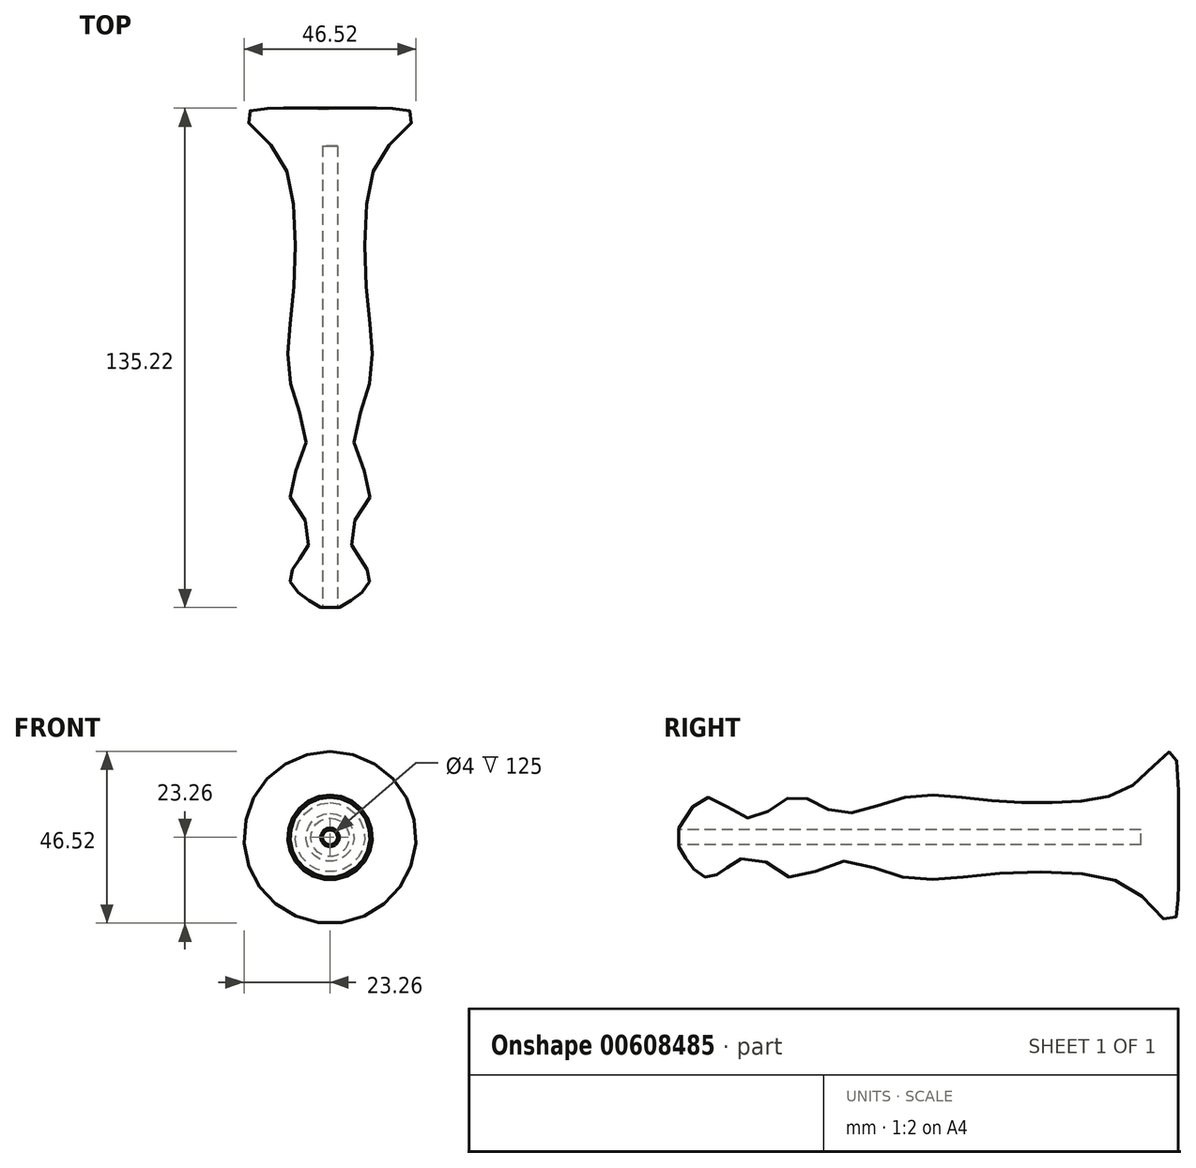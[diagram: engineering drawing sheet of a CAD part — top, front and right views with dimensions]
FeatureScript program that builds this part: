
annotation { "Feature Type Name" : "Feature", "Feature Type Description" : "" }
export const myFeature = defineFeature(function(context is Context, id is Id, definition is map)
    precondition{}
    {
        {
            var Q0;
            Q0=qCreatedBy(makeId("Right.planeOp"),FACE);
            var sketch = newSketch(context, id + "F0", { "sketchPlane" : qUnion([Q0])});
            skLineSegment(sketch, "E0", {"start": v(0, 0) * mm, "end": v(135, 0) * mm});
            skLineSegment(sketch, "E1", {"start": v(0, 0) * mm, "end": v(0, 2.5) * mm});
            skFitSpline(sketch, "E2", {"points": [v(0, 2.5) * mm, v(8.14, 10.8) * mm, v(19.4, 5.18) * mm, v(31.06, 11.1) * mm, v(42.9, 6.66) * mm, v(60.96, 10.8) * mm, v(82.5, 10.15) * mm, v(105.96, 9.62) * mm, v(124.31, 15.13) * mm, v(133.5, 23.2) * mm, v(135, 0) * mm], "startDerivative": vector(86.8, 151.46) * mm, "endDerivative": vector(-3.68, -254.52) * mm});
            skLineSegment(sketch, "E3", {"start": v(0, -19.1) * mm, "end": v(100.63, -19.1) * mm});
            skSolve(sketch);
        }
        {
            var Q0;
            Q0=makeQuery(id+"F0.imprint","IMPRINT",FACE,{"disambiguationData":[TD([[makeQuery(id+"F0.imprint","IMPRINT",EDGE,{"derivedFrom":sQuery(id+"F0.wireOp",EDGE,"E0")}),1.0]])]});
            var Q1;
            Q1=sQuery(id+"F0.wireOp",EDGE,"E0");
            revolve(context, id + "F1", {"entities" : qUnion([Q0]), "axis" : qUnion([Q1]), "revolveType" : RevolveType.FULL});
        }
        {
            var Q0;
            Q0=makeQuery(id+"F1.opRevolve","SWEPT_FACE",FACE,{"disambiguationData":[OSD([sQuery(id+"F0.wireOp",EDGE,"E1")])]});
            var sketch = newSketch(context, id + "F2", { "sketchPlane" : qUnion([Q0])});
            skCircle(sketch, "E4", {"center": v(0, 0) * mm, "radius": 2 * mm});
            skSolve(sketch);
        }
        {
            var Q0;
            Q0=makeQuery(id+"F2.imprint","IMPRINT",FACE,{"disambiguationData":[TD([[makeQuery(id+"F2.imprint","IMPRINT",EDGE,{"derivedFrom":sQuery(id+"F2.wireOp",EDGE,"E4")}),1.0]])]});
            extrude(context, id + "F3", {"entities" : qUnion([Q0]), "operationType" : NewBodyOperationType.REMOVE, "oppositeDirection" : true, "depth" : 125 * mm, "offsetDistance" : 25 * mm});
        }
    });
